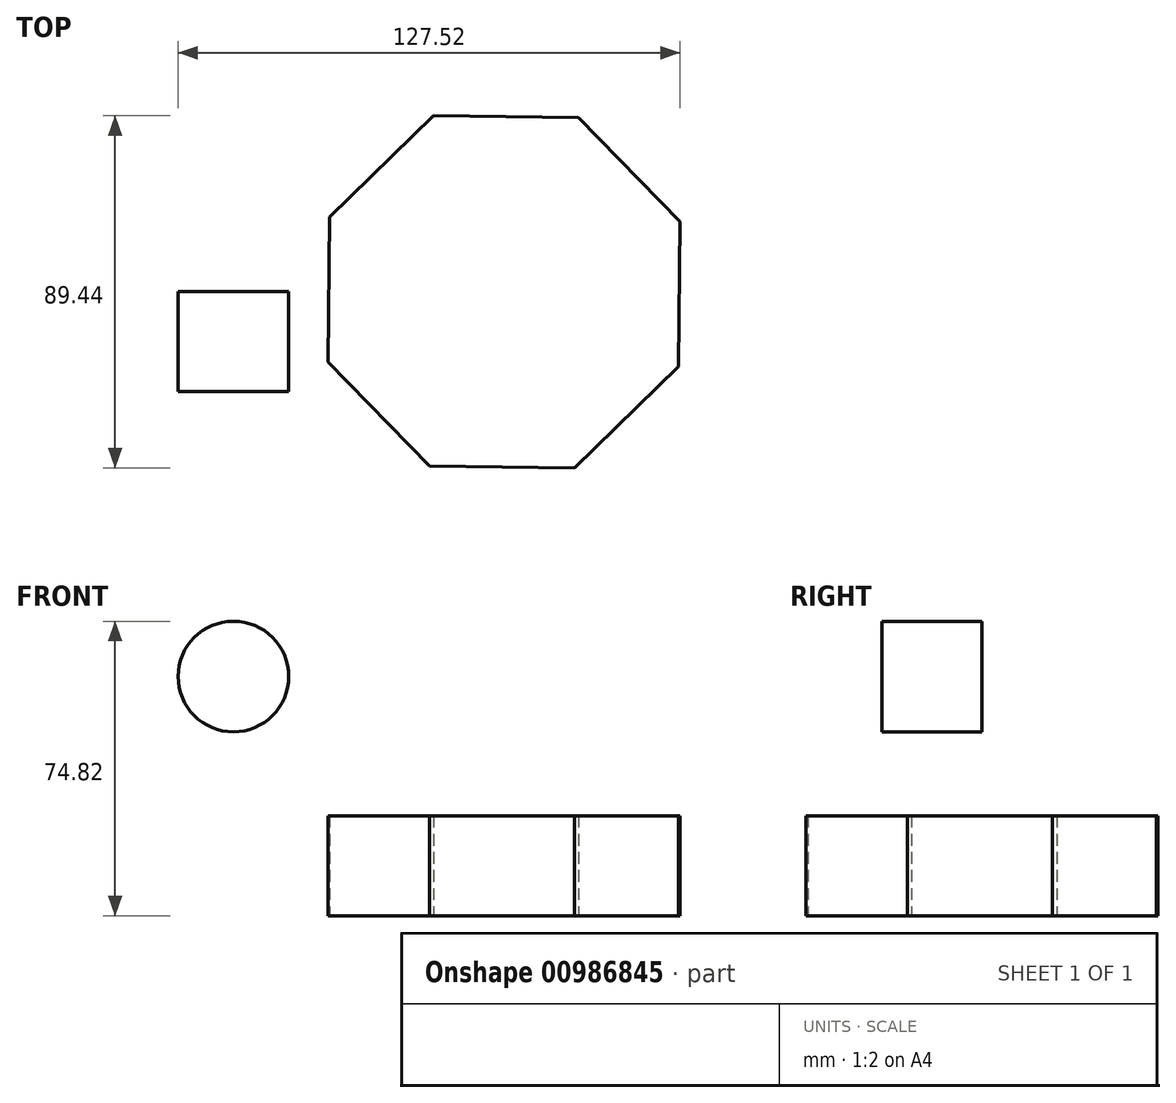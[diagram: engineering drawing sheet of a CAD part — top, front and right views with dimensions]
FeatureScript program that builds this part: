
annotation { "Feature Type Name" : "Feature", "Feature Type Description" : "" }
export const myFeature = defineFeature(function(context is Context, id is Id, definition is map)
    precondition{}
    {
        {
            var Q0;
            Q0=qCreatedBy(makeId("Top.planeOp"),FACE);
            var sketch = newSketch(context, id + "F0", { "sketchPlane" : qUnion([Q0])});
            skCircle(sketch, "E0.cCircle", {"center": v(0, 0) * mm, "radius": 44.5 * mm, "construction": true});
            skLineSegment(sketch, "E0.0", {"start": v(44.27, -18.97) * mm, "end": v(17.9, -44.72) * mm});
            skLineSegment(sketch, "E0.1", {"start": v(17.9, -44.72) * mm, "end": v(-18.97, -44.27) * mm});
            skLineSegment(sketch, "E0.2", {"start": v(-18.97, -44.27) * mm, "end": v(-44.72, -17.9) * mm});
            skLineSegment(sketch, "E0.3", {"start": v(-44.72, -17.9) * mm, "end": v(-44.27, 18.97) * mm});
            skLineSegment(sketch, "E0.4", {"start": v(-44.27, 18.97) * mm, "end": v(-17.9, 44.72) * mm});
            skLineSegment(sketch, "E0.5", {"start": v(-17.9, 44.72) * mm, "end": v(18.97, 44.27) * mm});
            skLineSegment(sketch, "E0.6", {"start": v(18.97, 44.27) * mm, "end": v(44.72, 17.9) * mm});
            skLineSegment(sketch, "E0.7", {"start": v(44.72, 17.9) * mm, "end": v(44.27, -18.97) * mm});
            skPoint(sketch, "E0.0.midPoint", {"position": v(31.08, -31.85) * mm});
            skSolve(sketch);
        }
        {
            var Q0;
            Q0=makeQuery(id+"F0.imprint","IMPRINT",FACE,{"disambiguationData":[TD([[makeQuery(id+"F0.imprint","IMPRINT",EDGE,{"derivedFrom":sQuery(id+"F0.wireOp",EDGE,"E0.0")}),-1.0]])]});
            extrude(context, id + "F1", {"entities" : qUnion([Q0]), "depth" : 25.4 * mm, "offsetDistance" : 25.4 * mm});
        }
        {
            var Q0;
            Q0=qCreatedBy(makeId("Front.planeOp"),FACE);
            var sketch = newSketch(context, id + "F2", { "sketchPlane" : qUnion([Q0])});
            skCircle(sketch, "E1", {"center": v(-68.75, 60.78) * mm, "radius": 14.05 * mm});
            skSolve(sketch);
        }
        {
            var Q0;
            Q0=makeQuery(id+"F2.imprint","IMPRINT",FACE,{"disambiguationData":[TD([[makeQuery(id+"F2.imprint","IMPRINT",EDGE,{"derivedFrom":sQuery(id+"F2.wireOp",EDGE,"E1")}),1.0]])]});
            extrude(context, id + "F3", {"entities" : qUnion([Q0]), "depth" : 25.4 * mm, "offsetDistance" : 25.4 * mm});
        }
    });
